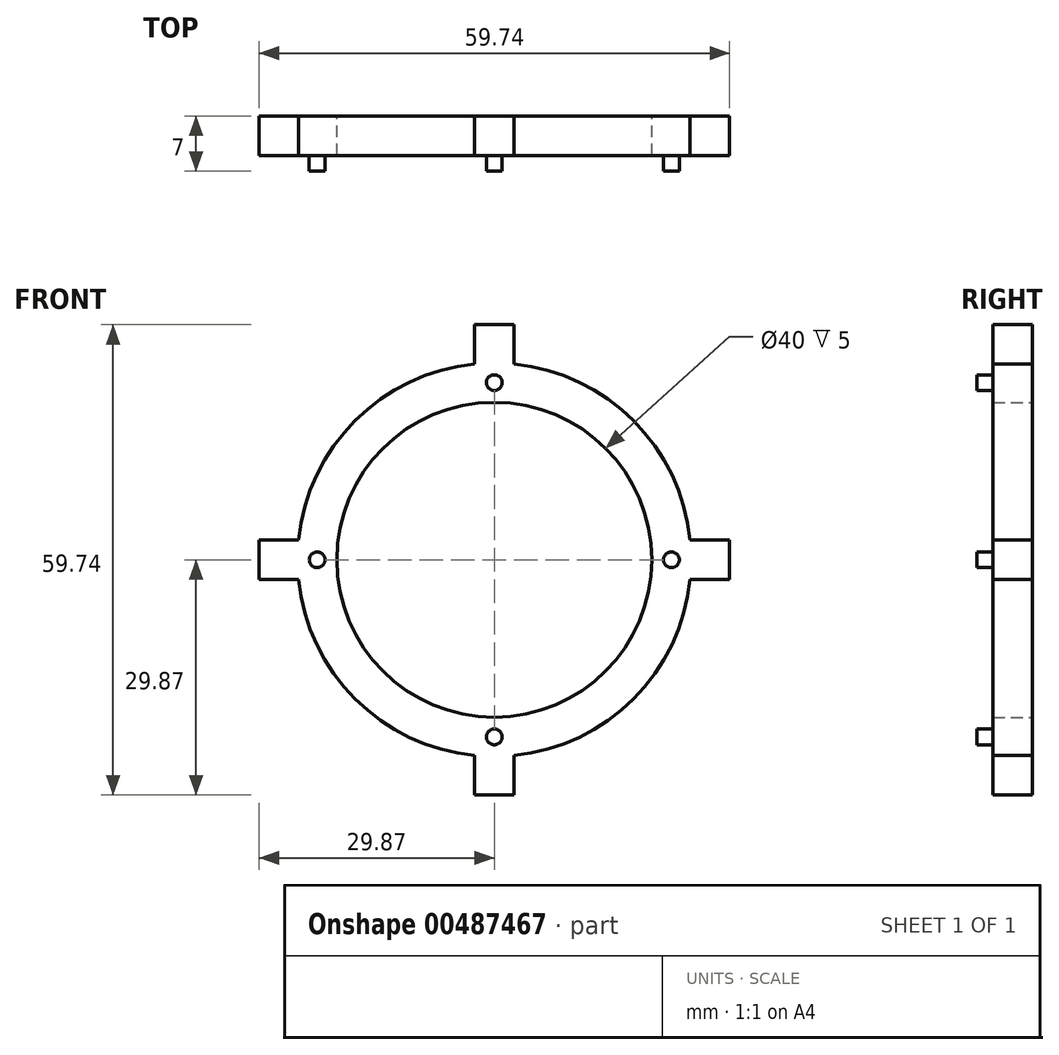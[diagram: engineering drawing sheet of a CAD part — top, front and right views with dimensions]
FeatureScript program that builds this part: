
annotation { "Feature Type Name" : "Feature", "Feature Type Description" : "" }
export const myFeature = defineFeature(function(context is Context, id is Id, definition is map)
    precondition{}
    {
        {
            var Q0;
            Q0=qCreatedBy(makeId("Front.planeOp"),FACE);
            var sketch = newSketch(context, id + "F0", { "sketchPlane" : qUnion([Q0])});
            skCircle(sketch, "E0", {"center": v(0, 0) * mm, "radius": 20 * mm});
            skCircle(sketch, "E1", {"center": v(0, 0) * mm, "radius": 25 * mm});
            skLineSegment(sketch, "E2.bottom", {"start": v(-2.5, 29.87) * mm, "end": v(2.5, 29.87) * mm});
            skLineSegment(sketch, "E2.top", {"start": v(-2.5, 24.87) * mm, "end": v(2.5, 24.87) * mm});
            skLineSegment(sketch, "E2.left", {"start": v(-2.5, 29.87) * mm, "end": v(-2.5, 24.87) * mm});
            skLineSegment(sketch, "E2.right", {"start": v(2.5, 29.87) * mm, "end": v(2.5, 24.87) * mm});
            skLineSegment(sketch, "E3.MirrorCS", {"start": v(-2.5, 29.87) * mm, "end": v(-7.5, 29.87) * mm});
            skLineSegment(sketch, "E4.MirrorCS", {"start": v(-2.5, -29.87) * mm, "end": v(-2.5, -24.87) * mm});
            skLineSegment(sketch, "E5.MirrorCS", {"start": v(-2.5, -29.87) * mm, "end": v(2.5, -29.87) * mm});
            skLineSegment(sketch, "E6.MirrorCS", {"start": v(2.5, -29.87) * mm, "end": v(2.5, -24.87) * mm});
            skLineSegment(sketch, "E7.bottom", {"start": v(24.87, 2.5) * mm, "end": v(29.87, 2.5) * mm});
            skLineSegment(sketch, "E7.top", {"start": v(24.87, -2.5) * mm, "end": v(29.87, -2.5) * mm});
            skLineSegment(sketch, "E7.left", {"start": v(24.87, 2.5) * mm, "end": v(24.87, -2.5) * mm});
            skLineSegment(sketch, "E7.right", {"start": v(29.87, 2.5) * mm, "end": v(29.87, -2.5) * mm});
            skLineSegment(sketch, "E8.MirrorCS", {"start": v(-24.87, 2.5) * mm, "end": v(-29.87, 2.5) * mm});
            skLineSegment(sketch, "E9.MirrorCS", {"start": v(-29.87, 2.5) * mm, "end": v(-29.87, -2.5) * mm});
            skLineSegment(sketch, "E10.MirrorCS", {"start": v(-24.87, -2.5) * mm, "end": v(-29.87, -2.5) * mm});
            skSolve(sketch);
        }
        {
            var Q0;
            Q0 = qSketchRegion(id + "F0", true);
            extrude(context, id + "F1", {"entities" : qUnion([Q0]), "depth" : 5 * mm});
        }
        {
            var Q0;
            Q0=qCreatedBy(makeId("Front.planeOp"),FACE);
            var sketch = newSketch(context, id + "F2", { "sketchPlane" : qUnion([Q0])});
            skCircle(sketch, "E11", {"center": v(0, 22.5) * mm, "radius": 1 * mm});
            skCircle(sketch, "E12.MirrorC", {"center": v(0, -22.5) * mm, "radius": 1 * mm});
            skCircle(sketch, "E13", {"center": v(22.5, 0) * mm, "radius": 1 * mm});
            skCircle(sketch, "E14.MirrorC", {"center": v(-22.5, 0) * mm, "radius": 1 * mm});
            skSolve(sketch);
        }
        {
            var Q0;
            Q0 = qSketchRegion(id + "F2", true);
            extrude(context, id + "F3", {"entities" : qUnion([Q0]), "operationType" : NewBodyOperationType.ADD, "depth" : 7 * mm});
        }
    });
